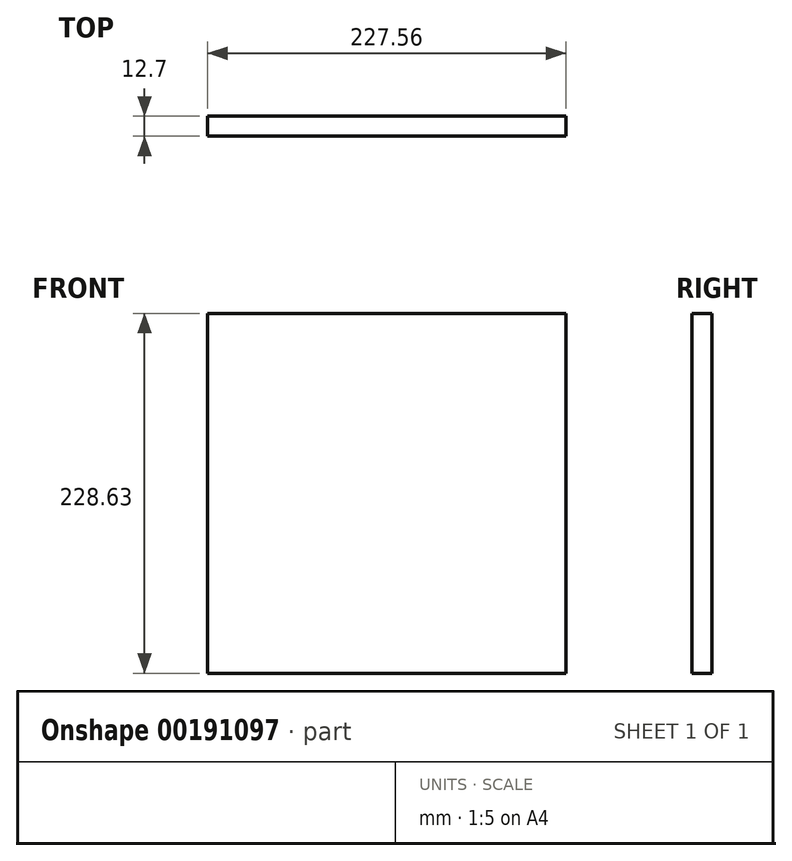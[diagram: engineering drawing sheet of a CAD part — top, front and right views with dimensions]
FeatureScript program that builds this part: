
annotation { "Feature Type Name" : "Feature", "Feature Type Description" : "" }
export const myFeature = defineFeature(function(context is Context, id is Id, definition is map)
    precondition{}
    {
        {
            var Q0;
            Q0=qCreatedBy(makeId("Front.planeOp"),FACE);
            var sketch = newSketch(context, id + "F0", { "sketchPlane" : qUnion([Q0])});
            skLineSegment(sketch, "E0.bottom", {"start": v(-124.37, -102.98) * mm, "end": v(103.2, -102.98) * mm});
            skLineSegment(sketch, "E0.top", {"start": v(-124.37, 125.65) * mm, "end": v(103.2, 125.65) * mm});
            skLineSegment(sketch, "E0.left", {"start": v(-124.37, -102.98) * mm, "end": v(-124.37, 125.65) * mm});
            skLineSegment(sketch, "E0.right", {"start": v(103.2, -102.98) * mm, "end": v(103.2, 125.65) * mm});
            skSolve(sketch);
        }
        {
            var Q0;
            Q0=makeQuery(id+"F0.imprint","IMPRINT",FACE,{"disambiguationData":[TD([[makeQuery(id+"F0.imprint","IMPRINT",EDGE,{"derivedFrom":sQuery(id+"F0.wireOp",EDGE,"E0.bottom")}),1.0]])]});
            var Q1;
            Q1 = qSketchRegion(id + "F0", true);
            extrude(context, id + "F1", {"entities" : qUnion([Q0, Q1]), "depth" : 12.7 * mm});
        }
    });
